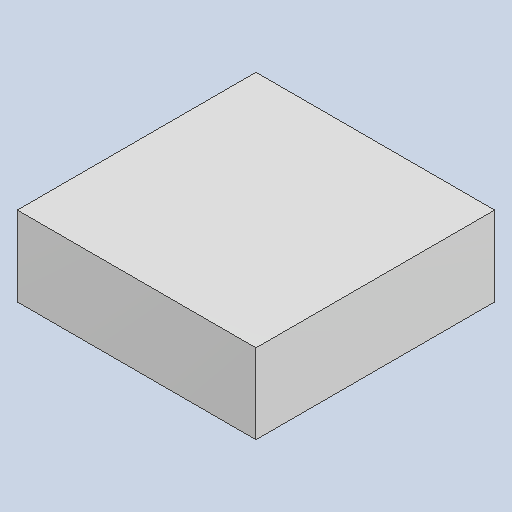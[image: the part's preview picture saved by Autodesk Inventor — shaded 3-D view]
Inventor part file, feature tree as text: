
AUTODESK INVENTOR PART (.ipt)
format: ipt  version: 2023.4 (Build 274418000, 418)  size: 79,872 bytes
history: native  units: mm
features: extrude x1
ambient origin geometry x8: Origin, YZ Plane, XZ Plane, XY Plane, X Axis, Y Axis, Z Axis, Center Point
bodies: Solid1 (feature_tree)
feature tree (1):
  extrude  "Extruded_65"  [1 undecoded]
note: 1 required parameter value undecoded (feature->parameter linkage not recoverable at this tier; creation-order binding heuristic only, values carry confidence <= 0.55)
